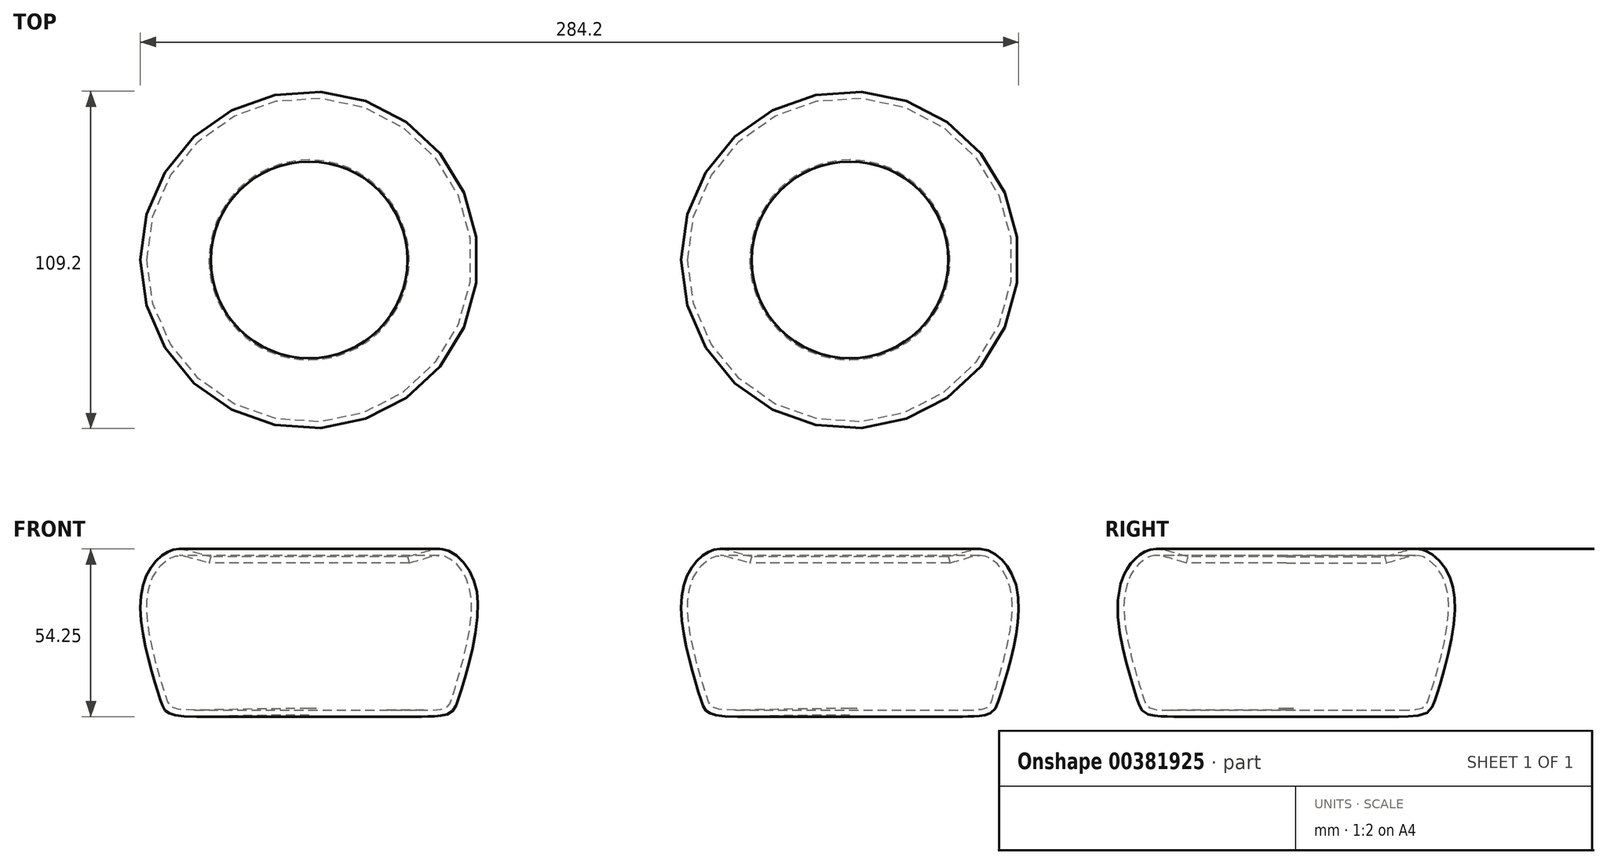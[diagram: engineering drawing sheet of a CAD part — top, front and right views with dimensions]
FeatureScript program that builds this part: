
annotation { "Feature Type Name" : "Feature", "Feature Type Description" : "" }
export const myFeature = defineFeature(function(context is Context, id is Id, definition is map)
    precondition{}
    {
        {
            var Q0;
            Q0=qCreatedBy(makeId("Front.planeOp"),FACE);
            var sketch = newSketch(context, id + "F0", { "sketchPlane" : qUnion([Q0])});
            skFitSpline(sketch, "E0", {"points": [v(0, 0) * mm, v(-48.52, 6) * mm, v(-54.23, 40) * mm, v(-44.7, 53.33) * mm, v(-31.84, 51.32) * mm], "startDerivative": vector(-412.28, 0) * mm, "endDerivative": vector(111.94, -30.53) * mm});
            skFitSpline(sketch, "E1.0", {"points": [v(0, 2.1) * mm, v(-4.3, 2.1) * mm, v(-12.1, 2.05) * mm, v(-21.61, 1.9) * mm, v(-29.18, 1.73) * mm, v(-35.01, 1.62) * mm, v(-39.34, 1.63) * mm, v(-41.83, 1.8) * mm, v(-43.23, 2.04) * mm, v(-43.98, 2.26) * mm, v(-44.48, 2.48) * mm, v(-44.8, 2.7) * mm, v(-45.05, 2.96) * mm, v(-45.31, 3.33) * mm, v(-45.6, 3.9) * mm, v(-45.9, 4.68) * mm, v(-46.16, 5.5) * mm, v(-46.4, 6.25) * mm, v(-46.66, 7.07) * mm, v(-47, 8.18) * mm, v(-47.61, 10.13) * mm, v(-48.44, 12.85) * mm, v(-49.47, 16.49) * mm, v(-50.46, 20.37) * mm, v(-51.33, 24.4) * mm, v(-52.02, 28.44) * mm, v(-52.45, 32.4) * mm, v(-52.53, 35.52) * mm, v(-52.4, 37.84) * mm, v(-52.21, 39.48) * mm, v(-51.9, 41) * mm, v(-51.37, 42.91) * mm, v(-50.47, 45.06) * mm, v(-49.13, 47.24) * mm, v(-47.62, 49) * mm, v(-46.3, 50.11) * mm, v(-45.26, 50.78) * mm, v(-44.52, 51.16) * mm, v(-43.82, 51.43) * mm, v(-43.17, 51.6) * mm, v(-42.53, 51.68) * mm, v(-41.64, 51.7) * mm, v(-40.32, 51.53) * mm, v(-38.29, 51.01) * mm, v(-35.71, 50.24) * mm, v(-33.58, 49.62) * mm, v(-32.4, 49.3) * mm]});
            skLineSegment(sketch, "E2", {"start": v(-32.4, 49.3) * mm, "end": v(-31.84, 51.32) * mm});
            skLineSegment(sketch, "E3", {"start": v(0, 2.1) * mm, "end": v(0, 0) * mm});
            skSolve(sketch);
        }
        {
            var Q0;
            Q0=makeQuery(id+"F0.imprint","IMPRINT",FACE,{"disambiguationData":[TD([[makeQuery(id+"F0.imprint","IMPRINT",EDGE,{"derivedFrom":sQuery(id+"F0.wireOp",EDGE,"E0")}),-1.0]])]});
            var Q1;
            Q1=sQuery(id+"F0.wireOp",EDGE,"E3");
            revolve(context, id + "F1", {"entities" : qUnion([Q0]), "axis" : qUnion([Q1]), "revolveType" : RevolveType.FULL});
        }
        {
            var Q0;
            Q0=makeQuery(id+"F1.opRevolve","SWEPT_BODY",BODY,{"disambiguationData":[OSD([sQuery(id+"F0.wireOp",EDGE,"E0"),sQuery(id+"F0.wireOp",EDGE,"E1.0"),sQuery(id+"F0.wireOp",EDGE,"E2"),sQuery(id+"F0.wireOp",EDGE,"E3")])]});
            transform(context, id + "F2", {"entities" : qUnion([Q0]), "transformType" : TransformType.TRANSLATION_3D, "dx" : 175 * mm, "dy" : 0 * mm, "dz" : 0 * mm, "makeCopy" : true});
        }
    });
